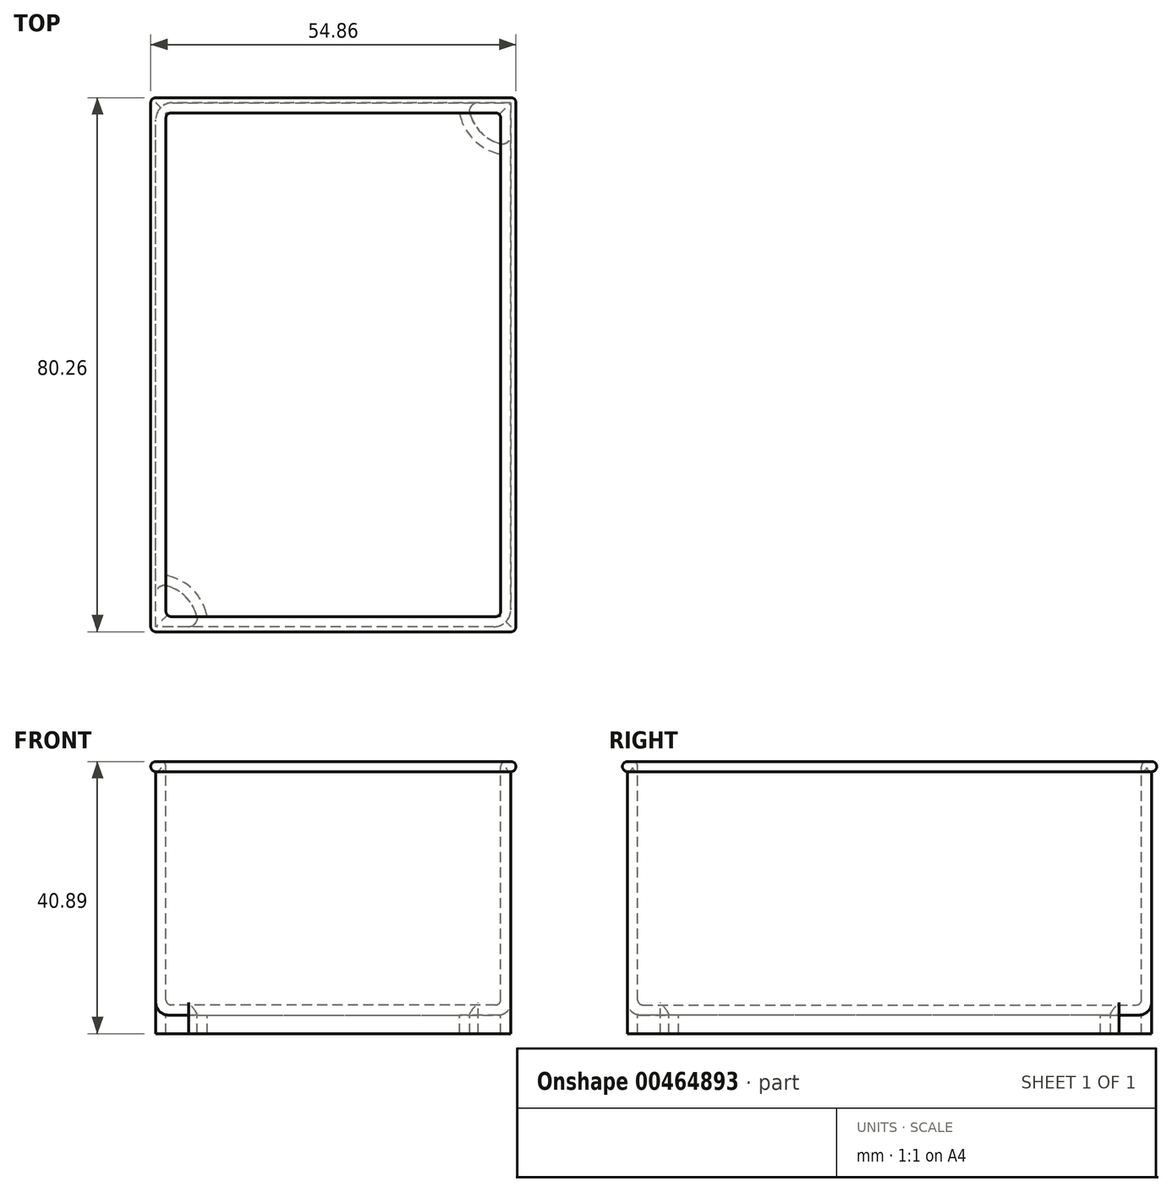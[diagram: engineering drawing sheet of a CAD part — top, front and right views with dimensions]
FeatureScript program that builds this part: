
annotation { "Feature Type Name" : "Feature", "Feature Type Description" : "" }
export const myFeature = defineFeature(function(context is Context, id is Id, definition is map)
    precondition{}
    {
        {
            var Q0;
            Q0=qCreatedBy(makeId("Front.planeOp"),FACE);
            var sketch = newSketch(context, id + "F0", { "sketchPlane" : qUnion([Q0])});
            skLineSegment(sketch, "E0.bottom", {"start": v(26.67, -19.05) * mm, "end": v(-26.67, -19.05) * mm});
            skLineSegment(sketch, "E0.top", {"start": v(26.67, 19.05) * mm, "end": v(-26.67, 19.05) * mm});
            skLineSegment(sketch, "E0.left", {"start": v(26.67, -19.05) * mm, "end": v(26.67, 19.05) * mm});
            skLineSegment(sketch, "E0.right", {"start": v(-26.67, -19.05) * mm, "end": v(-26.67, 19.05) * mm});
            skPoint(sketch, "E0.middle", {"position": v(0, 0) * mm});
            skSolve(sketch);
        }
        {
            var Q0;
            Q0=makeQuery(id+"F0.imprint","IMPRINT",FACE,{"disambiguationData":[TD([[makeQuery(id+"F0.imprint","IMPRINT",EDGE,{"derivedFrom":sQuery(id+"F0.wireOp",EDGE,"E0.bottom")}),-1.0]])]});
            extrude(context, id + "F1", {"entities" : qUnion([Q0]), "endBound" : BoundingType.SYMMETRIC, "depth" : 78.74 * mm});
        }
        {
            var Q0;
            Q0=makeQuery(id+"F1.opExtrude","SWEPT_FACE",FACE,{"disambiguationData":[OSD([sQuery(id+"F0.wireOp",EDGE,"E0.top")])]});
            shell(context, id + "F2", {"entities" : qUnion([Q0]), "thickness" : 1.52 * mm});
        }
        {
            var Q0;
            Q0=makeQuery(id+"F1.opExtrude","CAP_FACE",FACE,{"disambiguationData":[OSD([sQuery(id+"F0.wireOp",EDGE,"E0.bottom"),sQuery(id+"F0.wireOp",EDGE,"E0.top"),sQuery(id+"F0.wireOp",EDGE,"E0.left"),sQuery(id+"F0.wireOp",EDGE,"E0.right")])],"isStart":false});
            var sketch = newSketch(context, id + "F3", { "sketchPlane" : qUnion([Q0])});
            skArc(sketch, "E1", {"start": v(-26.67, 19.05) * mm, "mid": v(-27.43, 18.29) * mm, "end": v(-26.67, 17.53) * mm});
            skSolve(sketch);
        }
        {
            var Q0;
            {var subQ0=sQuery(id+"F3.wireOp",EDGE,"E1");Q0=makeQuery(id+"F3.imprint","IMPRINT",FACE,{"disambiguationData":[TD([[makeQuery(id+"F3.imprint","IMPRINT",EDGE,{"derivedFrom":subQ0}),1.0]])]});}
            var Q1;
            Q1=makeQuery(id+"F1.opExtrude","SWEPT_EDGE",EDGE,{"disambiguationData":[OSD([sQuery(id+"F0.wireOp",EDGE,"E0.top"),sQuery(id+"F0.wireOp",EDGE,"E0.right")])]});
            var Q2;
            Q2=makeQuery(id+"F1.opExtrude","CAP_EDGE",EDGE,{"disambiguationData":[OSD([sQuery(id+"F0.wireOp",EDGE,"E0.top")])],"isStart":true});
            var Q3;
            Q3=makeQuery(id+"F1.opExtrude","SWEPT_EDGE",EDGE,{"disambiguationData":[OSD([sQuery(id+"F0.wireOp",EDGE,"E0.top"),sQuery(id+"F0.wireOp",EDGE,"E0.left")])]});
            var Q4;
            Q4=makeQuery(id+"F1.opExtrude","CAP_EDGE",EDGE,{"disambiguationData":[OSD([sQuery(id+"F0.wireOp",EDGE,"E0.top")])],"isStart":false});
            sweep(context, id + "F4", {"operationType" : NewBodyOperationType.ADD, "profiles" : qUnion([Q0]), "path" : qUnion([Q1, Q2, Q3, Q4])});
        }
        {
            var Q0;
            Q0=makeQuery(id+"F1.opExtrude","SWEPT_FACE",FACE,{"disambiguationData":[OSD([sQuery(id+"F0.wireOp",EDGE,"E0.bottom")])]});
            var sketch = newSketch(context, id + "F5", { "sketchPlane" : qUnion([Q0])});
            skLineSegment(sketch, "E2.bottom", {"start": v(26.67, 39.37) * mm, "end": v(21.75, 39.37) * mm});
            skLineSegment(sketch, "E2.left", {"start": v(26.67, 39.37) * mm, "end": v(26.67, 34.45) * mm});
            skPoint(sketch, "E3.newPointA", {"position": v(20.32, 19.05) * mm});
            skArc(sketch, "E4", {"start": v(20.52, 37.78) * mm, "mid": v(22.18, 34.88) * mm, "end": v(25.08, 33.22) * mm});
            skPoint(sketch, "E5.visualSharp", {"position": v(20.32, 39.37) * mm});
            skArc(sketch, "E5.filletArc", {"start": v(21.75, 39.37) * mm, "mid": v(20.75, 38.88) * mm, "end": v(20.52, 37.78) * mm});
            skPoint(sketch, "E6.visualSharp", {"position": v(26.67, 33.02) * mm});
            skArc(sketch, "E6.filletArc", {"start": v(25.08, 33.22) * mm, "mid": v(26.18, 33.45) * mm, "end": v(26.67, 34.45) * mm});
            skArc(sketch, "E7.MirrorCS", {"start": v(-21.75, 39.37) * mm, "mid": v(-20.75, 38.88) * mm, "end": v(-20.52, 37.78) * mm});
            skArc(sketch, "E8.MirrorCS", {"start": v(-20.52, 37.78) * mm, "mid": v(-22.18, 34.88) * mm, "end": v(-25.08, 33.22) * mm});
            skArc(sketch, "E9.MirrorCS", {"start": v(-25.08, 33.22) * mm, "mid": v(-26.18, 33.45) * mm, "end": v(-26.67, 34.45) * mm});
            skLineSegment(sketch, "E10.MirrorCS", {"start": v(-26.67, 39.37) * mm, "end": v(-26.67, 34.45) * mm});
            skLineSegment(sketch, "E11.MirrorCS", {"start": v(-26.67, 39.37) * mm, "end": v(-21.75, 39.37) * mm});
            skArc(sketch, "E12.MirrorCS", {"start": v(-20.52, -37.78) * mm, "mid": v(-22.18, -34.88) * mm, "end": v(-25.08, -33.22) * mm});
            skArc(sketch, "E13.MirrorCS", {"start": v(-21.75, -39.37) * mm, "mid": v(-20.75, -38.88) * mm, "end": v(-20.52, -37.78) * mm});
            skLineSegment(sketch, "E14.MirrorCS", {"start": v(-26.67, -39.37) * mm, "end": v(-21.75, -39.37) * mm});
            skLineSegment(sketch, "E15.MirrorCS", {"start": v(-26.67, -39.37) * mm, "end": v(-26.67, -34.45) * mm});
            skArc(sketch, "E16.MirrorCS", {"start": v(-25.08, -33.22) * mm, "mid": v(-26.18, -33.45) * mm, "end": v(-26.67, -34.45) * mm});
            skArc(sketch, "E17.MirrorCS", {"start": v(21.75, -39.37) * mm, "mid": v(20.75, -38.88) * mm, "end": v(20.52, -37.78) * mm});
            skArc(sketch, "E18.MirrorCS", {"start": v(20.52, -37.78) * mm, "mid": v(22.18, -34.88) * mm, "end": v(25.08, -33.22) * mm});
            skArc(sketch, "E19.MirrorCS", {"start": v(25.08, -33.22) * mm, "mid": v(26.18, -33.45) * mm, "end": v(26.67, -34.45) * mm});
            skLineSegment(sketch, "E20.MirrorCS", {"start": v(26.67, -39.37) * mm, "end": v(26.67, -34.45) * mm});
            skLineSegment(sketch, "E21.MirrorCS", {"start": v(26.67, -39.37) * mm, "end": v(21.75, -39.37) * mm});
            skSolve(sketch);
        }
        {
            var Q0;
            Q0=makeQuery(id+"F5.imprint","IMPRINT",FACE,{"disambiguationData":[TD([[makeQuery(id+"F5.imprint","IMPRINT",EDGE,{"derivedFrom":sQuery(id+"F5.wireOp",EDGE,"E2.bottom")}),1.0]])]});
            var Q1;
            Q1=makeQuery(id+"F5.imprint","IMPRINT",FACE,{"disambiguationData":[TD([[makeQuery(id+"F5.imprint","IMPRINT",EDGE,{"derivedFrom":sQuery(id+"F5.wireOp",EDGE,"E8.MirrorCS")}),-1.0]])]});
            var Q2;
            Q2=makeQuery(id+"F5.imprint","IMPRINT",FACE,{"disambiguationData":[TD([[makeQuery(id+"F5.imprint","IMPRINT",EDGE,{"derivedFrom":sQuery(id+"F5.wireOp",EDGE,"E12.MirrorCS")}),1.0]])]});
            var Q3;
            Q3=makeQuery(id+"F5.imprint","IMPRINT",FACE,{"disambiguationData":[TD([[makeQuery(id+"F5.imprint","IMPRINT",EDGE,{"derivedFrom":sQuery(id+"F5.wireOp",EDGE,"E17.MirrorCS")}),-1.0]])]});
            extrude(context, id + "F6", {"entities" : qUnion([Q0, Q1, Q2, Q3]), "operationType" : NewBodyOperationType.ADD, "depth" : 2.8 * mm});
        }
        {
            var Q0;
            Q0=makeQuery(id+"F6.opExtrude","CAP_FACE",FACE,{"disambiguationData":[OSD([sQuery(id+"F5.wireOp",EDGE,"E2.bottom"),sQuery(id+"F5.wireOp",EDGE,"E2.left"),sQuery(id+"F5.wireOp",EDGE,"E4"),sQuery(id+"F5.wireOp",EDGE,"E5.filletArc"),sQuery(id+"F5.wireOp",EDGE,"E6.filletArc")])],"isStart":false});
            var Q1;
            Q1=makeQuery(id+"F6.opExtrude","CAP_FACE",FACE,{"disambiguationData":[OSD([sQuery(id+"F5.wireOp",EDGE,"E8.MirrorCS"),sQuery(id+"F5.wireOp",EDGE,"E9.MirrorCS"),sQuery(id+"F5.wireOp",EDGE,"E10.MirrorCS"),sQuery(id+"F5.wireOp",EDGE,"E7.MirrorCS"),sQuery(id+"F5.wireOp",EDGE,"E11.MirrorCS")])],"isStart":false});
            var Q2;
            Q2=makeQuery(id+"F6.opExtrude","CAP_FACE",FACE,{"disambiguationData":[OSD([sQuery(id+"F5.wireOp",EDGE,"E12.MirrorCS"),sQuery(id+"F5.wireOp",EDGE,"E13.MirrorCS"),sQuery(id+"F5.wireOp",EDGE,"E14.MirrorCS"),sQuery(id+"F5.wireOp",EDGE,"E15.MirrorCS"),sQuery(id+"F5.wireOp",EDGE,"E16.MirrorCS")])],"isStart":false});
            var Q3;
            Q3=makeQuery(id+"F6.opExtrude","CAP_FACE",FACE,{"disambiguationData":[OSD([sQuery(id+"F5.wireOp",EDGE,"E17.MirrorCS"),sQuery(id+"F5.wireOp",EDGE,"E18.MirrorCS"),sQuery(id+"F5.wireOp",EDGE,"E19.MirrorCS"),sQuery(id+"F5.wireOp",EDGE,"E20.MirrorCS"),sQuery(id+"F5.wireOp",EDGE,"E21.MirrorCS")])],"isStart":false});
            shell(context, id + "F7", {"entities" : qUnion([Q0, Q1, Q2, Q3]), "thickness" : 1.52 * mm});
        }
        {
            var Q0;
            Q0=makeQuery(id+"F2.opShell","OFFSET_FACE",FACE,{"disambiguationData":[OSD([sQuery(id+"F0.wireOp",EDGE,"E0.left")])]});
            var Q1;
            {var subQ0=sQuery(id+"F0.wireOp",EDGE,"E0.right");var subQ1=sQuery(id+"F0.wireOp",EDGE,"E0.left");var subQ2=sQuery(id+"F0.wireOp",EDGE,"E0.top");var subQ3=sQuery(id+"F0.wireOp",EDGE,"E0.bottom");Q1=makeQuery(id+"F2.opShell","OFFSET_FACE",FACE,{"disambiguationData":[OSD([subQ3,subQ2,subQ1,subQ0]),TDD([makeQuery(id+"F1.opExtrude","CAP_FACE",FACE,{"disambiguationData":[OSD([subQ3,subQ2,subQ1,subQ0])],"isStart":true})])]});}
            var Q2;
            Q2=makeQuery(id+"F2.opShell","OFFSET_FACE",FACE,{"disambiguationData":[OSD([sQuery(id+"F0.wireOp",EDGE,"E0.right")])]});
            var Q3;
            {var subQ0=sQuery(id+"F0.wireOp",EDGE,"E0.right");var subQ1=sQuery(id+"F0.wireOp",EDGE,"E0.left");var subQ2=sQuery(id+"F0.wireOp",EDGE,"E0.top");var subQ3=sQuery(id+"F0.wireOp",EDGE,"E0.bottom");Q3=makeQuery(id+"F2.opShell","OFFSET_FACE",FACE,{"disambiguationData":[OSD([subQ3,subQ2,subQ1,subQ0]),TDD([makeQuery(id+"F1.opExtrude","CAP_FACE",FACE,{"disambiguationData":[OSD([subQ3,subQ2,subQ1,subQ0])],"isStart":false})])]});}
            fillet(context, id + "F8", {"entities" : qUnion([Q0, Q1, Q2, Q3]), "radius" : 0.76 * mm, "tangentPropagation" : true, "allowEdgeOverflow" : false});
        }
        {
            var Q0;
            Q0=makeQuery(id+"F1.opExtrude","SWEPT_EDGE",EDGE,{"disambiguationData":[OSD([sQuery(id+"F0.wireOp",EDGE,"E0.bottom"),sQuery(id+"F0.wireOp",EDGE,"E0.right")])]});
            var Q1;
            Q1=makeQuery(id+"F1.opExtrude","CAP_EDGE",EDGE,{"disambiguationData":[OSD([sQuery(id+"F0.wireOp",EDGE,"E0.bottom")])],"isStart":false});
            var Q2;
            Q2=makeQuery(id+"F1.opExtrude","SWEPT_EDGE",EDGE,{"disambiguationData":[OSD([sQuery(id+"F0.wireOp",EDGE,"E0.bottom"),sQuery(id+"F0.wireOp",EDGE,"E0.left")])]});
            var Q3;
            Q3=makeQuery(id+"F1.opExtrude","CAP_EDGE",EDGE,{"disambiguationData":[OSD([sQuery(id+"F0.wireOp",EDGE,"E0.bottom")])],"isStart":true});
            fillet(context, id + "F9", {"entities" : qUnion([Q0, Q1, Q2, Q3]), "radius" : 1.9 * mm, "tangentPropagation" : true, "allowEdgeOverflow" : false});
        }
        {
            var Q0;
            Q0=makeQuery(id+"F4.opSweep","MID_CAP_EDGE",EDGE,{"disambiguationData":[OSD([sQuery(id+"F0.wireOp",EDGE,"E0.top"),sQuery(id+"F0.wireOp",EDGE,"E0.left"),sQuery(id+"F3.wireOp",EDGE,"E1")])],"capPos":3.0});
            var Q1;
            Q1=makeQuery(id+"F4.opSweep","MID_CAP_EDGE",EDGE,{"disambiguationData":[OSD([sQuery(id+"F0.wireOp",EDGE,"E0.top"),sQuery(id+"F0.wireOp",EDGE,"E0.left"),sQuery(id+"F3.wireOp",EDGE,"E1")])],"capPos":2.0});
            var Q2;
            Q2=makeQuery(id+"F4.opSweep","MID_CAP_EDGE",EDGE,{"disambiguationData":[OSD([sQuery(id+"F0.wireOp",EDGE,"E0.top"),sQuery(id+"F0.wireOp",EDGE,"E0.right"),sQuery(id+"F3.wireOp",EDGE,"E1")])],"capPos":1.0});
            var Q3;
            Q3=makeQuery(id+"F4.opSweep","CAP_EDGE",EDGE,{"disambiguationData":[OSD([sQuery(id+"F0.wireOp",EDGE,"E0.top"),sQuery(id+"F0.wireOp",EDGE,"E0.right"),sQuery(id+"F3.wireOp",EDGE,"E1")])],"isStart":true});
            fillet(context, id + "F10", {"entities" : qUnion([Q0, Q1, Q2, Q3]), "radius" : 0.76 * mm, "tangentPropagation" : true, "allowEdgeOverflow" : false});
        }
        {
            var Q0;
            Q0=makeQuery(id+"F6.boolean.opBoolean","MERGE",EDGE,{"derivedFrom":[makeQuery(id+"F1.opExtrude","CAP_EDGE",EDGE,{"disambiguationData":[OSD([sQuery(id+"F0.wireOp",EDGE,"E0.left")])],"isStart":false}),makeQuery(id+"F6.opExtrude","SWEPT_EDGE",EDGE,{"disambiguationData":[OSD([sQuery(id+"F5.wireOp",EDGE,"E2.bottom"),sQuery(id+"F5.wireOp",EDGE,"E2.left")])]})]});
            var Q1;
            Q1=makeQuery(id+"F6.boolean.opBoolean","MERGE",EDGE,{"derivedFrom":[makeQuery(id+"F1.opExtrude","CAP_EDGE",EDGE,{"disambiguationData":[OSD([sQuery(id+"F0.wireOp",EDGE,"E0.left")])],"isStart":true}),makeQuery(id+"F6.opExtrude","SWEPT_EDGE",EDGE,{"disambiguationData":[OSD([sQuery(id+"F5.wireOp",EDGE,"E20.MirrorCS"),sQuery(id+"F5.wireOp",EDGE,"E21.MirrorCS")])]})]});
            var Q2;
            Q2=makeQuery(id+"F6.boolean.opBoolean","MERGE",EDGE,{"derivedFrom":[makeQuery(id+"F1.opExtrude","CAP_EDGE",EDGE,{"disambiguationData":[OSD([sQuery(id+"F0.wireOp",EDGE,"E0.right")])],"isStart":false}),makeQuery(id+"F6.opExtrude","SWEPT_EDGE",EDGE,{"disambiguationData":[OSD([sQuery(id+"F5.wireOp",EDGE,"E10.MirrorCS"),sQuery(id+"F5.wireOp",EDGE,"E11.MirrorCS")])]})]});
            var Q3;
            Q3=makeQuery(id+"F6.boolean.opBoolean","MERGE",EDGE,{"derivedFrom":[makeQuery(id+"F1.opExtrude","CAP_EDGE",EDGE,{"disambiguationData":[OSD([sQuery(id+"F0.wireOp",EDGE,"E0.right")])],"isStart":true}),makeQuery(id+"F6.opExtrude","SWEPT_EDGE",EDGE,{"disambiguationData":[OSD([sQuery(id+"F5.wireOp",EDGE,"E14.MirrorCS"),sQuery(id+"F5.wireOp",EDGE,"E15.MirrorCS")])]})]});
            fillet(context, id + "F11", {"entities" : qUnion([Q0, Q1, Q2, Q3]), "radius" : 2.54 * mm, "tangentPropagation" : true, "allowEdgeOverflow" : false});
        }
    });
